# Revit family: VIESSMANN - Energycal AWH Pro AT 75-180
name_source: partatom
category: Wyposażenie mechaniczne
revit_build: Autodesk Revit 2017 (Build: 20160720_1515(x64)
units: mm (PartAtom-declared; Revit-internal decimal feet)

## family parameters
Numer OmniClass = 23.75.10.21.11
Oparty na płaszczyźnie roboczej = Nie
Punkt obliczania pomieszczeń = Nie
Tnij formami wycięć po wczytaniu = Nie
Typ części = Normalny
Tytuł OmniClass = Air-Source Heat Pumps
Współdzielony = Nie
Wymiar okrągłego złącza = Użyj średnicy
Zawsze pionowo = Tak

## types (6) — shared parameters
Autor = www.archispace.pl
Częstotliwość = 50 Hz
Głębokość = 1920 mm  [stored 6.29921 ft]
Ilość/Obiegi chłodnicze sprężarki (nr/nr) = 2/2
Liczba biegunów = 3
Moc nominalna wentylatora = 2 kW
Model = Powietrzna pompa ciepła Energycal AWH PRO AT / Air-water heat pump Energycal AWH PRO AT
Naczynie wzbiorcze = 18 m³
Napięcie zasilania = 400 V
Opis = Energycal AWH Pro AT to typoszereg wysokotemperaturowych pomp ciepła z czynnikiem chłodniczym R134a lub R513A osiągających na zasilaniu temperatury wody do 80°C.
Producent = Viessmann Sp. z o.o
Prąd nominalny wentylatora = 4 A
Stopień wydajności = 4
Strefa serwisowa_przód = 1000 mm  [stored 3.28084 ft]
Strefa serwisowa_szerokość = 1500 mm  [stored 4.92126 ft]
Strefa serwisowa_tył = 1000 mm  [stored 3.28084 ft]
Strefa serwisowa_wysokość = 1958 mm  [stored 6.42388 ft]
Typ sprężarki = Reciprocating
Typ wentylatora = Osiowy
Typ wymiennika po stronie grzewczej = Plate exchanger
URL = https://www.viessmann-projektant.pl
Viessmann Kolor 1 = Viessmann Kolor 2
Viessmann Kolor 2 = Viessmann Kolor 3
Współczynnik mocy = 1
Wysokość = 1958 mm  [stored 6.42388 ft]
Zasilanie elektryczne (V/ph/Hz) = 400/3N~/50+5%
Zasilanie pomocnicze (V/ph/Hz) = 230/1N~/50+5%

## per-type parameters (varying)
- Wielkość jednostki - 70: Całkowite napełnienie czynnikiem chłodniczym=27.00 kg; Całkowite napełnienie olejem=4.80 kg; Ciśnienie podnoszenia pompy (A7W45)=154.0 kPa; Efektywność sezonowa ηs=118%; Klasa energetyczna=A+; Liczba wentylatorów=2; Maksymalna moc pobierania=41 kW; Maksymalny pobór prądu=99 A; Maksymalny prąd rozruchowy=186 A; Moc nominalna silnika pompy obiegowej=1 kW; Natężenie przepływu wody (A7W45)=3.6 L/s; Natężenie przepływu wody (A7W45) l/h=12913; Nominalna moc grzewcza (A7W45)=75 kW; Nominalna moc pompy=1 kW; Obciążenie pozorne=41000 VA; Pobór mocy elektrycznej (A7W45)=22 kW; Pojemność zbiornika buforowego=250 m³; Poziom ciśnienia akustycznego - wersja cicha LN dB(A)=57 mm  [stored 0.187008 ft]; Poziom ciśnienia akustycznego - wersja super cicha SLN dB(A)=55 mm  [stored 0.180446 ft]; Poziom ciśnienia akustycznego dB(A)=59 mm; Poziom mocy akustycznej - wersja cicha LN dB(A)=89 mm  [stored 0.291995 ft]; Poziom mocy akustycznej - wersja super cicha SLN dB(A)=87 mm  [stored 0.285433 ft]; Poziom mocy akustycznej dB(A)=91 mm  [stored 0.298556 ft]; Połączenia hydrauliczne=2"; Przepływ powietrza=38500.0 m³/h; Przód=1671 mm  [stored 5.48228 ft]; Prąd nominalny silnika pompy obiegowej=2 A; SCOP=3.03; Spadek ciśnienia wody (A7W45)=17.0 kPa; Szerokość=3312 mm  [stored 10.8661 ft]; TYP=AWH PRO AT EVO 75-125; Tył=1654 mm  [stored 5.42651 ft]; Współczynnik efektywności [COP] (A7W45)=3.45
- Wielkość jednostki - 85: Całkowite napełnienie czynnikiem chłodniczym=27.00 kg; Całkowite napełnienie olejem=4.80 kg; Ciśnienie podnoszenia pompy (A7W45)=180.0 kPa; Efektywność sezonowa ηs=117.8 %; Klasa energetyczna=A+; Liczba wentylatorów=2; Maksymalna moc pobierania=50 kW; Maksymalny pobór prądu=105 A; Maksymalny prąd rozruchowy=189 A; Moc nominalna silnika pompy obiegowej=2 kW; Natężenie przepływu wody (A7W45)=4.3 L/s; Natężenie przepływu wody (A7W45) l/h=15347; Nominalna moc grzewcza (A7W45)=75 kW; Nominalna moc pompy=2 kW; Obciążenie pozorne=49800 VA; Pobór mocy elektrycznej (A7W45)=22 kW; Pojemność zbiornika buforowego=250 m³; Poziom ciśnienia akustycznego - wersja cicha LN dB(A)=57 mm  [stored 0.187008 ft]; Poziom ciśnienia akustycznego - wersja super cicha SLN dB(A)=55 mm  [stored 0.180446 ft]; Poziom ciśnienia akustycznego dB(A)=59 mm; Poziom mocy akustycznej - wersja cicha LN dB(A)=89 mm  [stored 0.291995 ft]; Poziom mocy akustycznej - wersja super cicha SLN dB(A)=87 mm  [stored 0.285433 ft]; Poziom mocy akustycznej dB(A)=91 mm  [stored 0.298556 ft]; Połączenia hydrauliczne=2"; Przepływ powietrza=40100.0 m³/h; Przód=1671 mm  [stored 5.48228 ft]; Prąd nominalny silnika pompy obiegowej=3 A; SCOP=3.02; Spadek ciśnienia wody (A7W45)=23.0 kPa; Szerokość=3312 mm  [stored 10.8661 ft]; TYP=AWH PRO AT EVO 75-125; Tył=1654 mm  [stored 5.42651 ft]; Współczynnik efektywności [COP] (A7W45)=3.45
- Wielkość jednostki - 105: Całkowite napełnienie czynnikiem chłodniczym=33.00 kg; Całkowite napełnienie olejem=9.50 kg; Ciśnienie podnoszenia pompy (A7W45)=154.0 kPa; Efektywność sezonowa ηs=115.1 %; Klasa energetyczna=A+; Liczba wentylatorów=2; Maksymalna moc pobierania=59 kW; Maksymalny pobór prądu=129 A; Maksymalny prąd rozruchowy=238 A; Moc nominalna silnika pompy obiegowej=2 kW; Natężenie przepływu wody (A7W45)=5.3 L/s; Natężenie przepływu wody (A7W45) l/h=18982; Nominalna moc grzewcza (A7W45)=110 kW; Nominalna moc pompy=2 kW; Obciążenie pozorne=59200 VA; Pobór mocy elektrycznej (A7W45)=32 kW; Pojemność zbiornika buforowego=250 m³; Poziom ciśnienia akustycznego - wersja cicha LN dB(A)=58 mm  [stored 0.190289 ft]; Poziom ciśnienia akustycznego - wersja super cicha SLN dB(A)=56 mm  [stored 0.183727 ft]; Poziom ciśnienia akustycznego dB(A)=60 mm  [stored 0.19685 ft]; Poziom mocy akustycznej - wersja cicha LN dB(A)=90 mm  [stored 0.295276 ft]; Poziom mocy akustycznej - wersja super cicha SLN dB(A)=88 mm  [stored 0.288714 ft]; Poziom mocy akustycznej dB(A)=92 mm  [stored 0.301837 ft]; Połączenia hydrauliczne=2"; Przepływ powietrza=40000.0 m³/h; Przód=1655 mm  [stored 5.42979 ft]; Prąd nominalny silnika pompy obiegowej=3 A; SCOP=2.95; Spadek ciśnienia wody (A7W45)=22.0 kPa; Szerokość=3312 mm  [stored 10.8661 ft]; TYP=AWH PRO AT EVO 75-125; Tył=1655 mm  [stored 5.42979 ft]; Współczynnik efektywności [COP] (A7W45)=3.47
- Wielkość jednostki - 125: Całkowite napełnienie czynnikiem chłodniczym=33.00 kg; Całkowite napełnienie olejem=9.50 kg; Ciśnienie podnoszenia pompy (A7W45)=170.0 kPa; Efektywność sezonowa ηs=125.6 %; Klasa energetyczna=A++; Liczba wentylatorów=2; Maksymalna moc pobierania=70 kW; Maksymalny pobór prądu=141 A; Maksymalny prąd rozruchowy=244 A; Moc nominalna silnika pompy obiegowej=2 kW; Natężenie przepływu wody (A7W45)=6.1 L/s; Natężenie przepływu wody (A7W45) l/h=21942; Nominalna moc grzewcza (A7W45)=127 kW; Nominalna moc pompy=3 kW; Obciążenie pozorne=70100 VA; Pobór mocy elektrycznej (A7W45)=36 kW; Pojemność zbiornika buforowego=250 m³; Poziom ciśnienia akustycznego - wersja cicha LN dB(A)=58 mm  [stored 0.190289 ft]; Poziom ciśnienia akustycznego - wersja super cicha SLN dB(A)=56 mm  [stored 0.183727 ft]; Poziom ciśnienia akustycznego dB(A)=60 mm  [stored 0.19685 ft]; Poziom mocy akustycznej - wersja cicha LN dB(A)=90 mm  [stored 0.295276 ft]; Poziom mocy akustycznej - wersja super cicha SLN dB(A)=88 mm  [stored 0.288714 ft]; Poziom mocy akustycznej dB(A)=92 mm  [stored 0.301837 ft]; Połączenia hydrauliczne=2"; Przepływ powietrza=42800.0 m³/h; Przód=1670 mm; Prąd nominalny silnika pompy obiegowej=5 A; SCOP=3.21; Spadek ciśnienia wody (A7W45)=18.0 kPa; Szerokość=3312 mm  [stored 10.8661 ft]; TYP=AWH PRO AT EVO 75-125; Tył=1655 mm  [stored 5.42979 ft]; Współczynnik efektywności [COP] (A7W45)=3.48
- Wielkość jednostki - 145: Całkowite napełnienie czynnikiem chłodniczym=38.00 kg; Całkowite napełnienie olejem=9.50 kg; Ciśnienie podnoszenia pompy (A7W45)=156.0 kPa; Efektywność sezonowa ηs=112.4 %; Klasa energetyczna=A+; Liczba wentylatorów=4; Maksymalna moc pobierania=86 kW; Maksymalny pobór prądu=168 A; Maksymalny prąd rozruchowy=281 A; Moc nominalna silnika pompy obiegowej=2 kW; Natężenie przepływu wody (A7W45)=6.9 L/s; Natężenie przepływu wody (A7W45) l/h=24765; Nominalna moc grzewcza (A7W45)=143 kW; Nominalna moc pompy=3 kW; Obciążenie pozorne=85900 VA; Pobór mocy elektrycznej (A7W45)=45 kW; Pojemność zbiornika buforowego=450 m³; Poziom ciśnienia akustycznego - wersja cicha LN dB(A)=59 mm; Poziom ciśnienia akustycznego - wersja super cicha SLN dB(A)=57 mm  [stored 0.187008 ft]; Poziom ciśnienia akustycznego dB(A)=61 mm  [stored 0.200131 ft]; Poziom mocy akustycznej - wersja cicha LN dB(A)=91 mm  [stored 0.298556 ft]; Poziom mocy akustycznej - wersja super cicha SLN dB(A)=89 mm  [stored 0.291995 ft]; Poziom mocy akustycznej dB(A)=93 mm  [stored 0.305118 ft]; Połączenia hydrauliczne=2 1/2"; Przepływ powietrza=91100.0 m³/h; Przód=2756 mm; Prąd nominalny silnika pompy obiegowej=5 A; SCOP=2.88; Spadek ciśnienia wody (A7W45)=19.0 kPa; Szerokość=4410 mm  [stored 14.4685 ft]; TYP=AWH PRO AT EVO 145-180; Tył=1657 mm; Współczynnik efektywności [COP] (A7W45)=3.19
- Wielkość jednostki - 180: Całkowite napełnienie czynnikiem chłodniczym=38.00 kg; Całkowite napełnienie olejem=9.50 kg; Ciśnienie podnoszenia pompy (A7W45)=185.0 kPa; Efektywność sezonowa ηs=118.6 %; Klasa energetyczna=A+; Liczba wentylatorów=4; Maksymalna moc pobierania=97 kW; Maksymalny pobór prądu=204 A; Maksymalny prąd rozruchowy=343 A; Moc nominalna silnika pompy obiegowej=3 kW; Natężenie przepływu wody (A7W45)=8.1 L/s; Natężenie przepływu wody (A7W45) l/h=29038; Nominalna moc grzewcza (A7W45)=168 kW; Nominalna moc pompy=3 kW; Obciążenie pozorne=96700 VA; Pobór mocy elektrycznej (A7W45)=49 kW; Pojemność zbiornika buforowego=450 m³; Poziom ciśnienia akustycznego - wersja cicha LN dB(A)=59 mm; Poziom ciśnienia akustycznego - wersja super cicha SLN dB(A)=57 mm  [stored 0.187008 ft]; Poziom ciśnienia akustycznego dB(A)=61 mm  [stored 0.200131 ft]; Poziom mocy akustycznej - wersja cicha LN dB(A)=91 mm  [stored 0.298556 ft]; Poziom mocy akustycznej - wersja super cicha SLN dB(A)=89 mm  [stored 0.291995 ft]; Poziom mocy akustycznej dB(A)=93 mm  [stored 0.305118 ft]; Połączenia hydrauliczne=2 1/2"; Przepływ powietrza=92500.0 m³/h; Przód=2756 mm; Prąd nominalny silnika pompy obiegowej=6 A; SCOP=3.04; Spadek ciśnienia wody (A7W45)=21.0 kPa; Szerokość=4410 mm  [stored 14.4685 ft]; TYP=AWH PRO AT EVO 145-180; Tył=1657 mm; Współczynnik efektywności [COP] (A7W45)=3.41

note: [stored X ft] marks values corroborated as IEEE doubles in the binary element streams (Revit-internal decimal feet)
